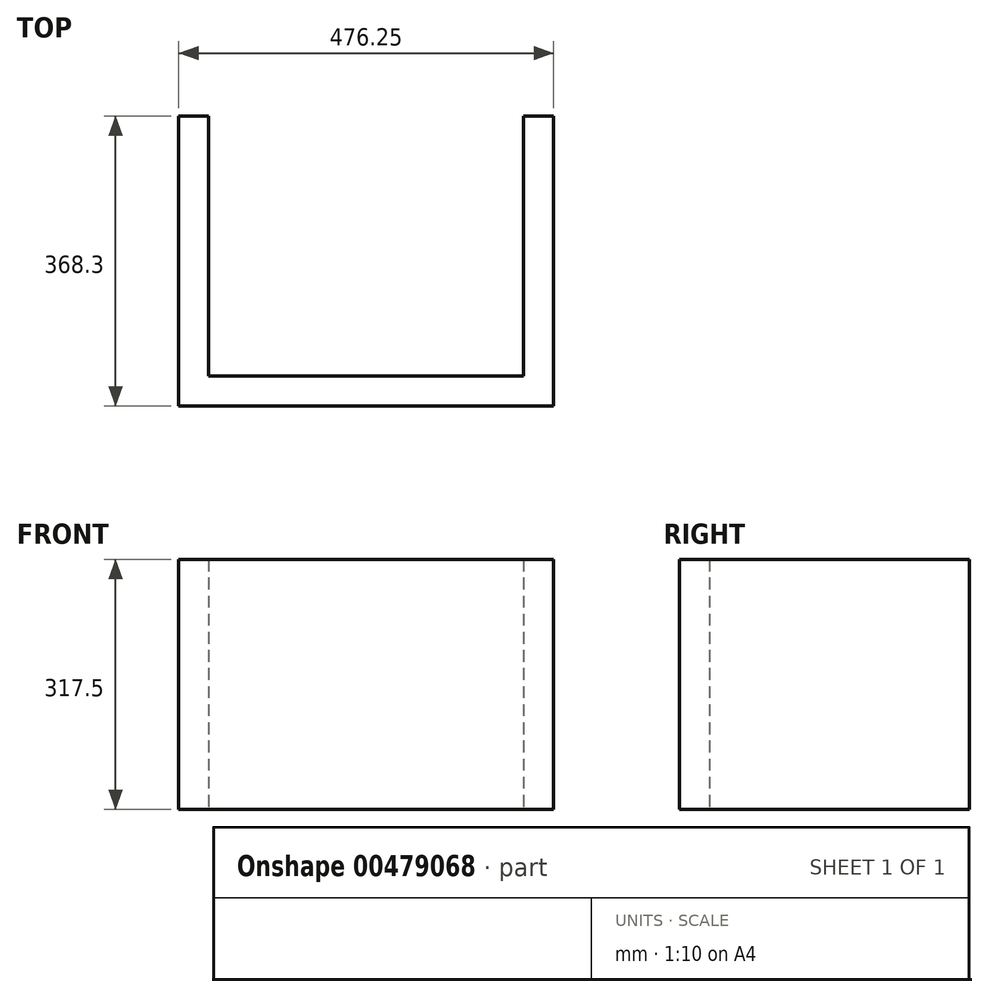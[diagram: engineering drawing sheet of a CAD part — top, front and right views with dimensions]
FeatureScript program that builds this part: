
annotation { "Feature Type Name" : "Feature", "Feature Type Description" : "" }
export const myFeature = defineFeature(function(context is Context, id is Id, definition is map)
    precondition{}
    {
        {
            var Q0;
            Q0=qCreatedBy(makeId("Top.planeOp"),FACE);
            var sketch = newSketch(context, id + "F0", { "sketchPlane" : qUnion([Q0])});
            skLineSegment(sketch, "E0", {"start": v(0, 0) * mm, "end": v(0, -368.3) * mm});
            skLineSegment(sketch, "E1", {"start": v(0, -368.3) * mm, "end": v(476.25, -368.3) * mm});
            skLineSegment(sketch, "E2", {"start": v(476.25, -368.3) * mm, "end": v(476.25, 0) * mm});
            skLineSegment(sketch, "E3", {"start": v(476.25, 0) * mm, "end": v(438.15, 0) * mm});
            skLineSegment(sketch, "E4", {"start": v(438.15, 0) * mm, "end": v(438.15, -330.2) * mm});
            skLineSegment(sketch, "E5", {"start": v(0, 0) * mm, "end": v(38.1, 0) * mm});
            skLineSegment(sketch, "E6", {"start": v(38.1, 0) * mm, "end": v(38.1, -330.2) * mm});
            skLineSegment(sketch, "E7", {"start": v(38.1, -330.2) * mm, "end": v(438.15, -330.2) * mm});
            skSolve(sketch);
        }
        {
            var Q0;
            Q0=makeQuery(id+"F0.imprint","IMPRINT",FACE,{"disambiguationData":[TD([[makeQuery(id+"F0.imprint","IMPRINT",EDGE,{"derivedFrom":sQuery(id+"F0.wireOp",EDGE,"E0")}),1.0]])]});
            extrude(context, id + "F1", {"entities" : qUnion([Q0]), "depth" : 317.5 * mm});
        }
    });
